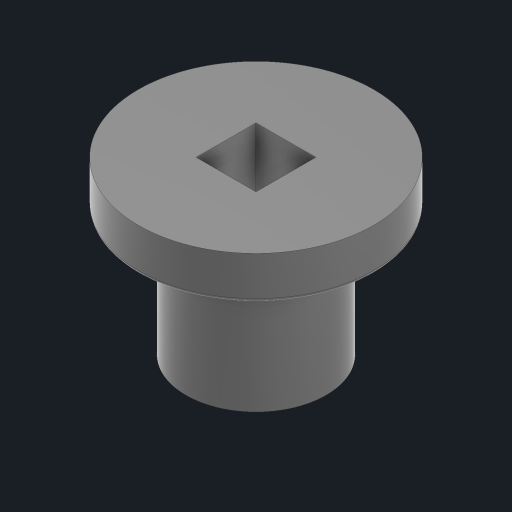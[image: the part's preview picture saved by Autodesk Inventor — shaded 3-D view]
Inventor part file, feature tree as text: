
AUTODESK INVENTOR PART (.ipt)
format: ipt  version: 2023 (Build 270158030, 158C)  size: 350,720 bytes
history: native  units: in
note: dims shown in document units (in); Inventor stores cm internally (conversion verified against a paired STEP export)
features: fillet x1
ambient origin geometry x8: Origin, YZ Plane, XZ Plane, XY Plane, X Axis, Y Axis, Z Axis, Center Point
bodies: Solid1 (feature_tree)
feature tree (1):
  fillet  "Fillet1"  [1 undecoded]
note: 1 required parameter value undecoded (feature->parameter linkage not recoverable at this tier; creation-order binding heuristic only, values carry confidence <= 0.55)
